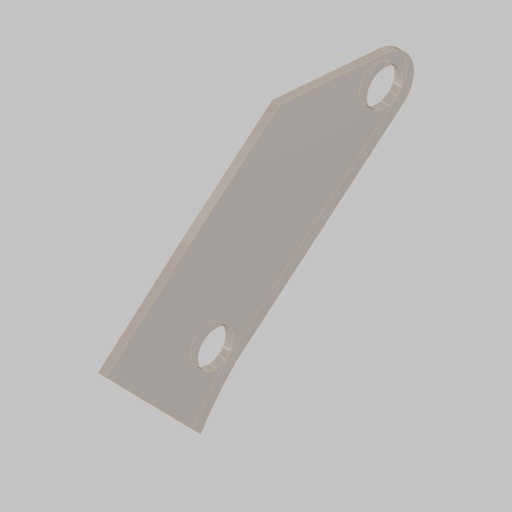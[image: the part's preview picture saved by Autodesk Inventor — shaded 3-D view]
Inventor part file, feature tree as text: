
AUTODESK INVENTOR PART (.ipt)
format: ipt  version: 2023.5 (Build 275446000, 446)  size: 163,840 bytes
history: native  units: in
note: dims shown in document units (in); Inventor stores cm internally (conversion verified against a paired STEP export)
features: sketch x4, extrude x2, hole x1, projected_geometry x1
ambient origin geometry x8: Origin, YZ Plane, XZ Plane, XY Plane, X Axis, Y Axis, Z Axis, Center Point
bodies: Body1 (feature_tree)
feature tree (8):
  sketch  "Sketch1"  dims[d0=16.0in d1=3.0in]
  extrude  "Extrusion2"  Depth=3.0in
  hole  "Hole2"  [1 undecoded]
  extrude  "Extrusion3"  Depth=7.0in
  sketch  "Sketch4"  dims[d2=0.25in d4=4.5in]
  sketch  "Sketch5"  dims[d5=11.875in d6=7.0in]
  sketch  "Sketch6"  dims[d27=1.125in d29=0.375in d31=4.0in d33=4.0in d35=3.75in d36=0.25in d37=0.0in d39=0.5in d41=0.201in d42=0.75in d43=0.385in d44=0.25in d45=0.5635in d46=1.0in d47=0.8108in d51=6.5in d52=11.0in d53=1.2075in d57=1.0in d58=11.75in d59=12.75in d60=1.25in d61=30.0deg d62=1.0in d63=0.0in]
  projected_geometry  "Projected Loop1"
note: 1 required parameter value undecoded (feature->parameter linkage not recoverable at this tier; creation-order binding heuristic only, values carry confidence <= 0.55)
